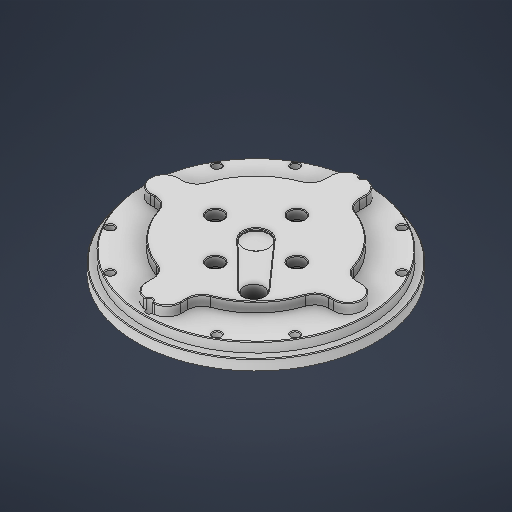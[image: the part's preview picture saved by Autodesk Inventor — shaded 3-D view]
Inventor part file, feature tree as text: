
AUTODESK INVENTOR PART (.ipt)
format: ipt  version: 2025 (Build 290162000, 162)  size: 665,600 bytes
history: native  units: in
note: dims shown in document units (in); Inventor stores cm internally (conversion verified against a paired STEP export)
features: sketch x18, extrude x12, hole x4, chamfer x4
ambient origin geometry x8: Origin, YZ Plane, XZ Plane, XY Plane, X Axis, Y Axis, Z Axis, Center Point
bodies: Solid1 (feature_tree)
feature tree (38):
  sketch  "Sketch1"  dims[d3=4.3307in d24=6.6929in]
  extrude  "Extrusion1"  Depth=6.6929in
  extrude  "Extrusion2"  Depth=5.9843in
  extrude  "Extrusion3"  Depth=4.3307in
  sketch  "Sketch2"  dims[d27=0.9843in d28=4.3307in]
  extrude  "Extrusion4"  Depth=0.3937in
  hole  "Hole1"  [1 undecoded]
  hole  "Hole2"  [1 undecoded]
  sketch  "Sketch4"  dims[d38=0.2953in d39=0.0in d40=2.2835in]
  extrude  "Extrusion5"  Depth=2.2835in
  extrude  "Extrusion6"  Depth=0.1969in
  hole  "Hole3"  [1 undecoded]
  chamfer  "Chamfer1"  Distance=0.7874in Angle=360.0deg
  chamfer  "Chamfer2"  Distance=0.0591in
  hole  "Hole5"  [1 undecoded]
  sketch  "Sketch9"  dims[d69=3.1496in]
  extrude  "Extrusion9"  Depth=0.3051in TaperAngle=45.0deg
  extrude  "Extrusion10"  Depth=0.3051in TaperAngle=45.0deg
  chamfer  "Chamfer4"  Distance=3.7402in
  sketch  "Sketch11"  dims[d74=0.4724in d75=0.0in d76=0.1969in]
  extrude  "Extrusion11"  Depth=0.3051in
  extrude  "Extrusion12"  Depth=0.3051in TaperAngle=360.0deg
  extrude  "Extrusion13"  Depth=0.3051in
  extrude  "Extrusion15"  Depth=0.3051in
  chamfer  "Chamfer6"  Distance=0.7185in
  sketch  "Sketch Circular Pattern1"  dims[d25=6.2992in d26=5.9843in]
  sketch  "Sketch3"  dims[d31=0.3937in d32=0.3937in]
  sketch  "Sketch Circular Pattern2"  dims[d29=0.7874in d30=0.3937in]
  sketch  "Sketch5"  dims[d41=0.4331in d42=0.1969in]
  sketch  "Sketch Circular Pattern3"  dims[d34=0.8465in d35=0.0in d36=0.5709in d37=0.0in]
  sketch  "Sketch7"  dims[d56=5.9843in]
  sketch  "Sketch Circular Pattern5"  dims[d43=1.5748in d45=360.0deg d47=0.2657in d48=0.0in]
  sketch  "Sketch Circular Pattern6"  dims[d49=0.2165in d50=0.7874in d51=0.1575in d52=0.0787in d53=90.0deg d54=0.315in d55=0.8108in]
  sketch  "Sketch10"  dims[d71=0.7874in d72=0.0591in d73=0.0in]
  sketch  "Sketch Circular Pattern7"  dims[d57=0.1378in d58=0.7874in d60=360.0deg]
  sketch  "Sketch Circular Pattern8"  dims[d62=0.1772in d63=0.315in d64=0.1575in d65=0.0787in d66=90.0deg d67=0.4646in d68=0.8108in]
  sketch  "Sketch Circular Pattern9"  dims[d70=0.1969in]
  sketch  "Sketch12"  dims[d77=4.7244in d79=360.0deg d81=0.2165in d82=0.3937in d83=0.1575in d84=0.0787in d85=90.0deg d86=0.3937in d87=0.8108in d88=0.0197in d89=0.0787in d90=45.0deg d91=0.0197in d92=0.0787in d93=45.0deg d107=3.7402in d108=0.1969in d109=6.2992in d111=360.0deg d113=0.1969in d114=0.7874in d115=0.748in d116=0.3543in d117=90.0deg d118=0.7874in d119=0.8108in d139=0.7185in d140=3.1496in d141=0.7185in d142=3.1496in d144=360.0deg d146=0.0689in d147=0.0in d151=0.5512in d152=1.7717in d153=0.0in d154=0.0in d155=0.0197in d156=0.0787in d157=45.0deg d158=0.5512in d159=1.7717in d160=0.3453in d161=4.7244in d163=360.0deg d165=0.3051in d166=0.7874in d168=360.0deg d170=0.3159in d171=1.5748in d173=360.0deg d175=0.1673in d176=0.0in d177=0.1575in d178=0.0in d179=0.1673in d180=0.0in d181=1.7717in d187=0.3117in d188=0.0492in d189=0.0in d190=0.0197in d191=0.0787in d192=45.0deg d137=0.0197in d138=0.0344in]
note: 4 required parameter values undecoded (feature->parameter linkage not recoverable at this tier; creation-order binding heuristic only, values carry confidence <= 0.55)
